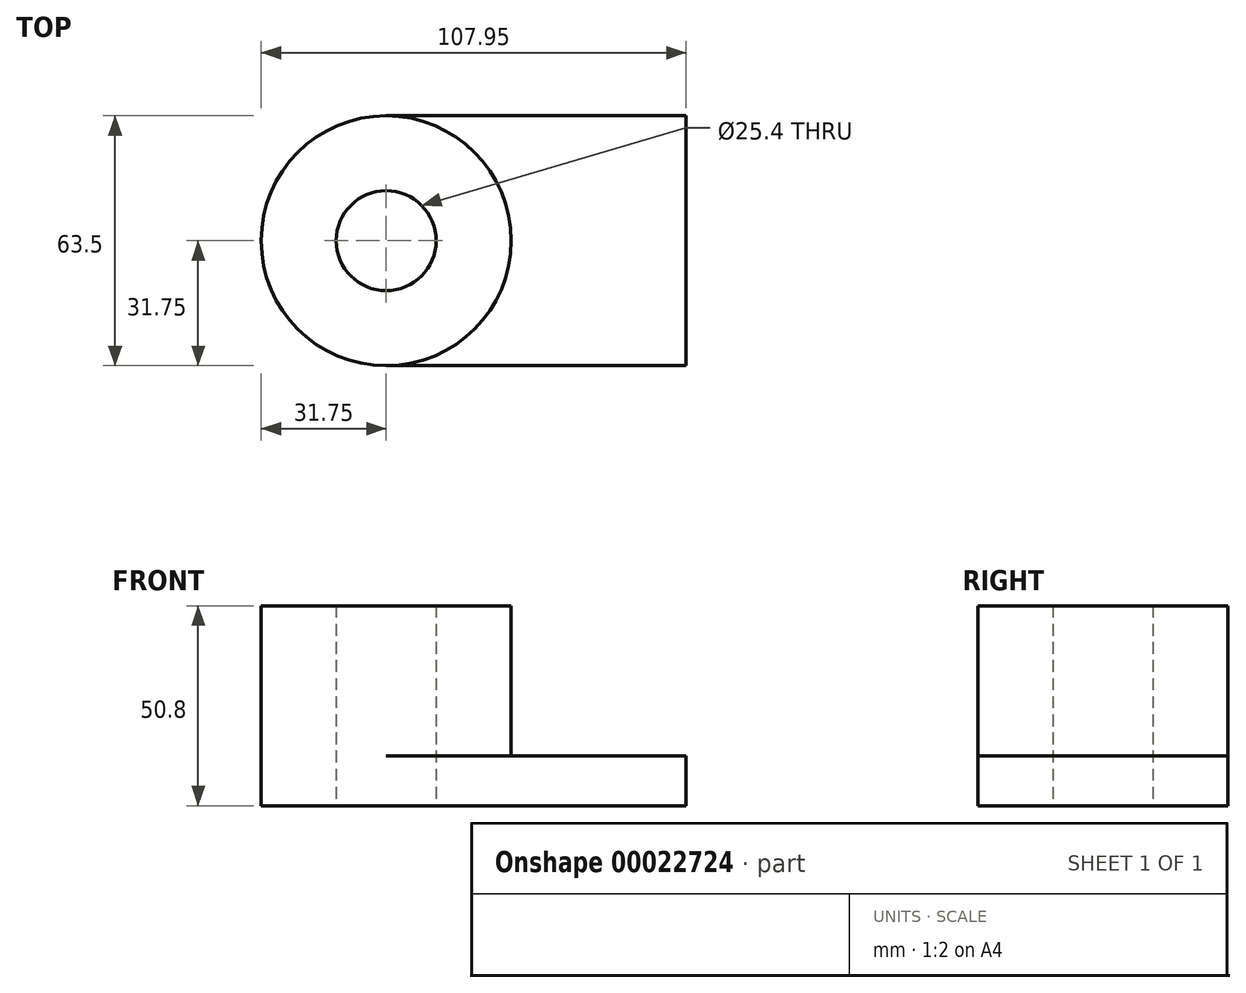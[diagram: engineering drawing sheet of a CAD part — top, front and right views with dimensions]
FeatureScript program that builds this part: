
annotation { "Feature Type Name" : "Feature", "Feature Type Description" : "" }
export const myFeature = defineFeature(function(context is Context, id is Id, definition is map)
    precondition{}
    {
        {
            var Q0;
            Q0=qCreatedBy(makeId("Top.planeOp"),FACE);
            var sketch = newSketch(context, id + "F0", { "sketchPlane" : qUnion([Q0])});
            skLineSegment(sketch, "E0.rect.bottom", {"start": v(-38.1, -31.75) * mm, "end": v(38.1, -31.75) * mm});
            skLineSegment(sketch, "E0.rect.top", {"start": v(-38.1, 31.75) * mm, "end": v(38.1, 31.75) * mm});
            skLineSegment(sketch, "E0.rect.left", {"start": v(-38.1, -31.75) * mm, "end": v(-38.1, 31.75) * mm});
            skLineSegment(sketch, "E0.rect.right", {"start": v(38.1, -31.75) * mm, "end": v(38.1, 31.75) * mm});
            skPoint(sketch, "E0.rect.middle", {"position": v(0, 0) * mm});
            skCircle(sketch, "E1", {"center": v(-38.1, 0) * mm, "radius": 31.75 * mm});
            skCircle(sketch, "E2", {"center": v(-38.1, 0) * mm, "radius": 12.7 * mm});
            skSolve(sketch);
        }
        {
            var Q0;
            Q0 = qSketchRegion(id + "F0", true);
            extrude(context, id + "F1", {"entities" : qUnion([Q0]), "depth" : 12.7 * mm});
        }
        {
            var Q0;
            {var subQ0=sQuery(id+"F0.wireOp",EDGE,"E2");var subQ1=sQuery(id+"F0.wireOp",EDGE,"E0.rect.left");var subQ3=makeQuery(id+"F0.imprint","INTERSECT",VERTEX,{"disambiguationData":[OD(0.0)],"derivedFrom":[subQ1,subQ0]});Q0=makeQuery(id+"F0.imprint","IMPRINT",FACE,{"disambiguationData":[TD([[makeQuery(id+"F0.imprint","IMPRINT",EDGE,{"disambiguationData":[TD([[subQ3,-1.0]])],"derivedFrom":subQ0}),-1.0]])]});}
            var Q1;
            {var subQ0=sQuery(id+"F0.wireOp",EDGE,"E2");var subQ1=sQuery(id+"F0.wireOp",EDGE,"E0.rect.left");var subQ3=makeQuery(id+"F0.imprint","INTERSECT",VERTEX,{"disambiguationData":[OD(0.0)],"derivedFrom":[subQ1,subQ0]});Q1=makeQuery(id+"F0.imprint","IMPRINT",FACE,{"disambiguationData":[TD([[makeQuery(id+"F0.imprint","IMPRINT",EDGE,{"disambiguationData":[TD([[subQ3,1.0]])],"derivedFrom":subQ0}),-1.0]])]});}
            extrude(context, id + "F2", {"entities" : qUnion([Q0, Q1]), "operationType" : NewBodyOperationType.ADD, "depth" : 50.8 * mm});
        }
    });
